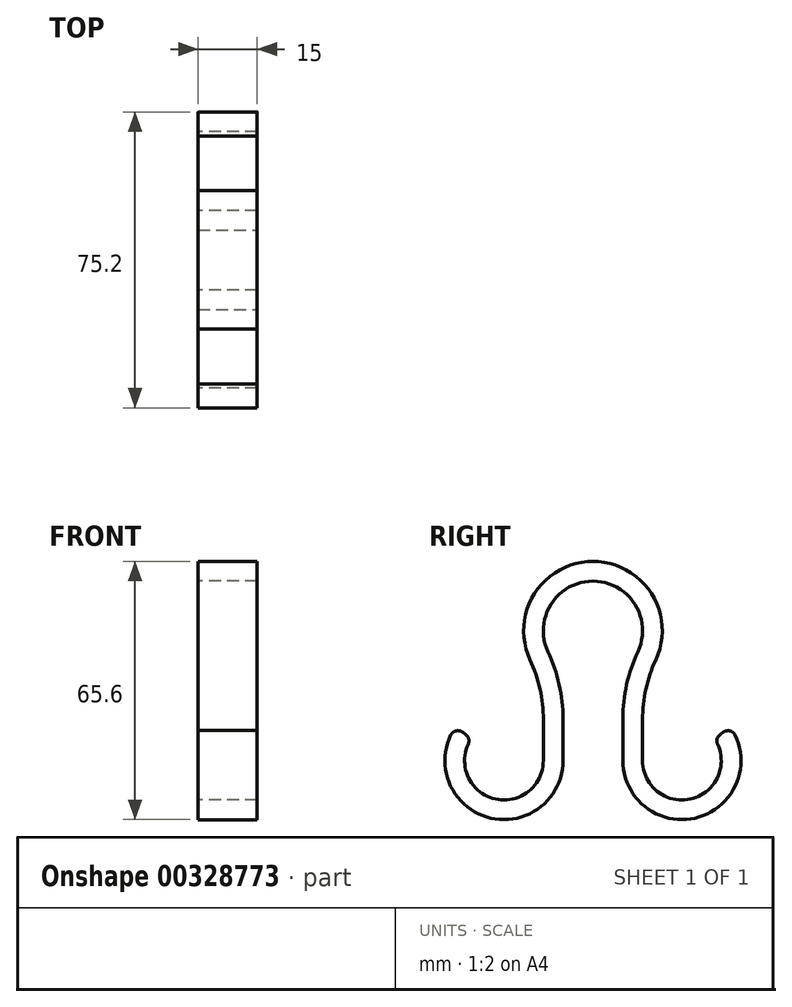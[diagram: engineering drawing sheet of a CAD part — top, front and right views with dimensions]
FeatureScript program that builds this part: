
annotation { "Feature Type Name" : "Feature", "Feature Type Description" : "" }
export const myFeature = defineFeature(function(context is Context, id is Id, definition is map)
    precondition{}
    {
        {
            var Q0;
            Q0=qCreatedBy(makeId("Right.planeOp"),FACE);
            var sketch = newSketch(context, id + "F0", { "sketchPlane" : qUnion([Q0])});
            skCircle(sketch, "E0", {"center": v(0, 0) * mm, "radius": 12.5 * mm, "construction": true});
            skSolve(sketch);
        }
        {
            var Q0;
            Q0=qCreatedBy(makeId("Right.planeOp"),FACE);
            var sketch = newSketch(context, id + "F1", { "sketchPlane" : qUnion([Q0])});
            skArc(sketch, "E1", {"start": v(7.6, -10.05) * mm, "mid": v(0, 12.6) * mm, "end": v(-7.6, -10.05) * mm});
            skLineSegment(sketch, "E2", {"start": v(0, 0) * mm, "end": v(0, 15.55) * mm, "construction": true});
            skLineSegment(sketch, "E3", {"start": v(-7.6, -3.8) * mm, "end": v(-7.6, -59.95) * mm, "construction": true});
            skLineSegment(sketch, "E4", {"start": v(7.6, 5.06) * mm, "end": v(7.6, -50.82) * mm, "construction": true});
            skLineSegment(sketch, "E5", {"start": v(-12.6, 0) * mm, "end": v(-12.6, -50.82) * mm, "construction": true});
            skLineSegment(sketch, "E6", {"start": v(-7.6, -10.05) * mm, "end": v(-7.6, -33) * mm});
            skArc(sketch, "E7", {"start": v(-7.6, -33) * mm, "mid": v(-27.04, -47.33) * mm, "end": v(-34.98, -24.53) * mm});
            skLineSegment(sketch, "E8", {"start": v(0, 0) * mm, "end": v(-22.6, -33) * mm, "construction": true});
            skLineSegment(sketch, "E9", {"start": v(-22.6, -33) * mm, "end": v(-39.1, -21.7) * mm, "construction": true});
            skArc(sketch, "E10.0", {"start": v(-12.6, -33) * mm, "mid": v(-25.56, -42.56) * mm, "end": v(-30.85, -27.35) * mm});
            skLineSegment(sketch, "E10.1", {"start": v(-12.6, -12.29) * mm, "end": v(-12.6, -33) * mm});
            skArc(sketch, "E10.2", {"start": v(12.6, -12.29) * mm, "mid": v(0, 17.6) * mm, "end": v(-12.6, -12.29) * mm});
            skLineSegment(sketch, "E11", {"start": v(-30.85, -27.35) * mm, "end": v(-34.98, -24.53) * mm});
            skLineSegment(sketch, "E12.MirrorCS", {"start": v(12.6, -12.29) * mm, "end": v(12.6, -33) * mm});
            skLineSegment(sketch, "E13.MirrorCS", {"start": v(30.85, -27.35) * mm, "end": v(34.98, -24.53) * mm});
            skLineSegment(sketch, "E14.MirrorCS", {"start": v(7.6, -10.05) * mm, "end": v(7.6, -33) * mm});
            skArc(sketch, "E15.MirrorCS", {"start": v(12.6, -33) * mm, "mid": v(25.56, -42.56) * mm, "end": v(30.85, -27.35) * mm});
            skArc(sketch, "E16.MirrorCS", {"start": v(7.6, -33) * mm, "mid": v(27.04, -47.33) * mm, "end": v(34.98, -24.53) * mm});
            skSolve(sketch);
        }
        {
            var Q0;
            Q0 = qSketchRegion(id + "F1", true);
            extrude(context, id + "F2", {"entities" : qUnion([Q0]), "depth" : 15 * mm});
        }
        {
            var Q0;
            Q0=makeQuery(id+"F2.opExtrude","SWEPT_EDGE",EDGE,{"disambiguationData":[OSD([sQuery(id+"F1.wireOp",EDGE,"E10.2"),sQuery(id+"F1.wireOp",EDGE,"E12.MirrorCS")])]});
            var Q1;
            Q1=makeQuery(id+"F2.opExtrude","SWEPT_EDGE",EDGE,{"disambiguationData":[OSD([sQuery(id+"F1.wireOp",EDGE,"E10.1"),sQuery(id+"F1.wireOp",EDGE,"E10.2")])]});
            fillet(context, id + "F3", {"entities" : qUnion([Q0, Q1]), "radius" : 36 * mm, "tangentPropagation" : true, "allowEdgeOverflow" : false});
        }
        {
            var Q0;
            Q0=makeQuery(id+"F2.opExtrude","SWEPT_EDGE",EDGE,{"disambiguationData":[OSD([sQuery(id+"F1.wireOp",EDGE,"E1"),sQuery(id+"F1.wireOp",EDGE,"E14.MirrorCS")])]});
            var Q1;
            Q1=makeQuery(id+"F2.opExtrude","SWEPT_EDGE",EDGE,{"disambiguationData":[OSD([sQuery(id+"F1.wireOp",EDGE,"E1"),sQuery(id+"F1.wireOp",EDGE,"E6")])]});
            fillet(context, id + "F4", {"entities" : qUnion([Q0, Q1]), "radius" : 40 * mm, "tangentPropagation" : true, "allowEdgeOverflow" : false});
        }
        {
            var Q0;
            Q0=makeQuery(id+"F2.opExtrude","SWEPT_EDGE",EDGE,{"disambiguationData":[OSD([sQuery(id+"F1.wireOp",EDGE,"E13.MirrorCS"),sQuery(id+"F1.wireOp",EDGE,"E15.MirrorCS")])]});
            var Q1;
            Q1=makeQuery(id+"F2.opExtrude","SWEPT_EDGE",EDGE,{"disambiguationData":[OSD([sQuery(id+"F1.wireOp",EDGE,"E13.MirrorCS"),sQuery(id+"F1.wireOp",EDGE,"E16.MirrorCS")])]});
            var Q2;
            Q2=makeQuery(id+"F2.opExtrude","SWEPT_EDGE",EDGE,{"disambiguationData":[OSD([sQuery(id+"F1.wireOp",EDGE,"E10.0"),sQuery(id+"F1.wireOp",EDGE,"E11")])]});
            var Q3;
            Q3=makeQuery(id+"F2.opExtrude","SWEPT_EDGE",EDGE,{"disambiguationData":[OSD([sQuery(id+"F1.wireOp",EDGE,"E7"),sQuery(id+"F1.wireOp",EDGE,"E11")])]});
            fillet(context, id + "F5", {"entities" : qUnion([Q0, Q1, Q2, Q3]), "radius" : 2 * mm, "tangentPropagation" : true, "allowEdgeOverflow" : false});
        }
    });
